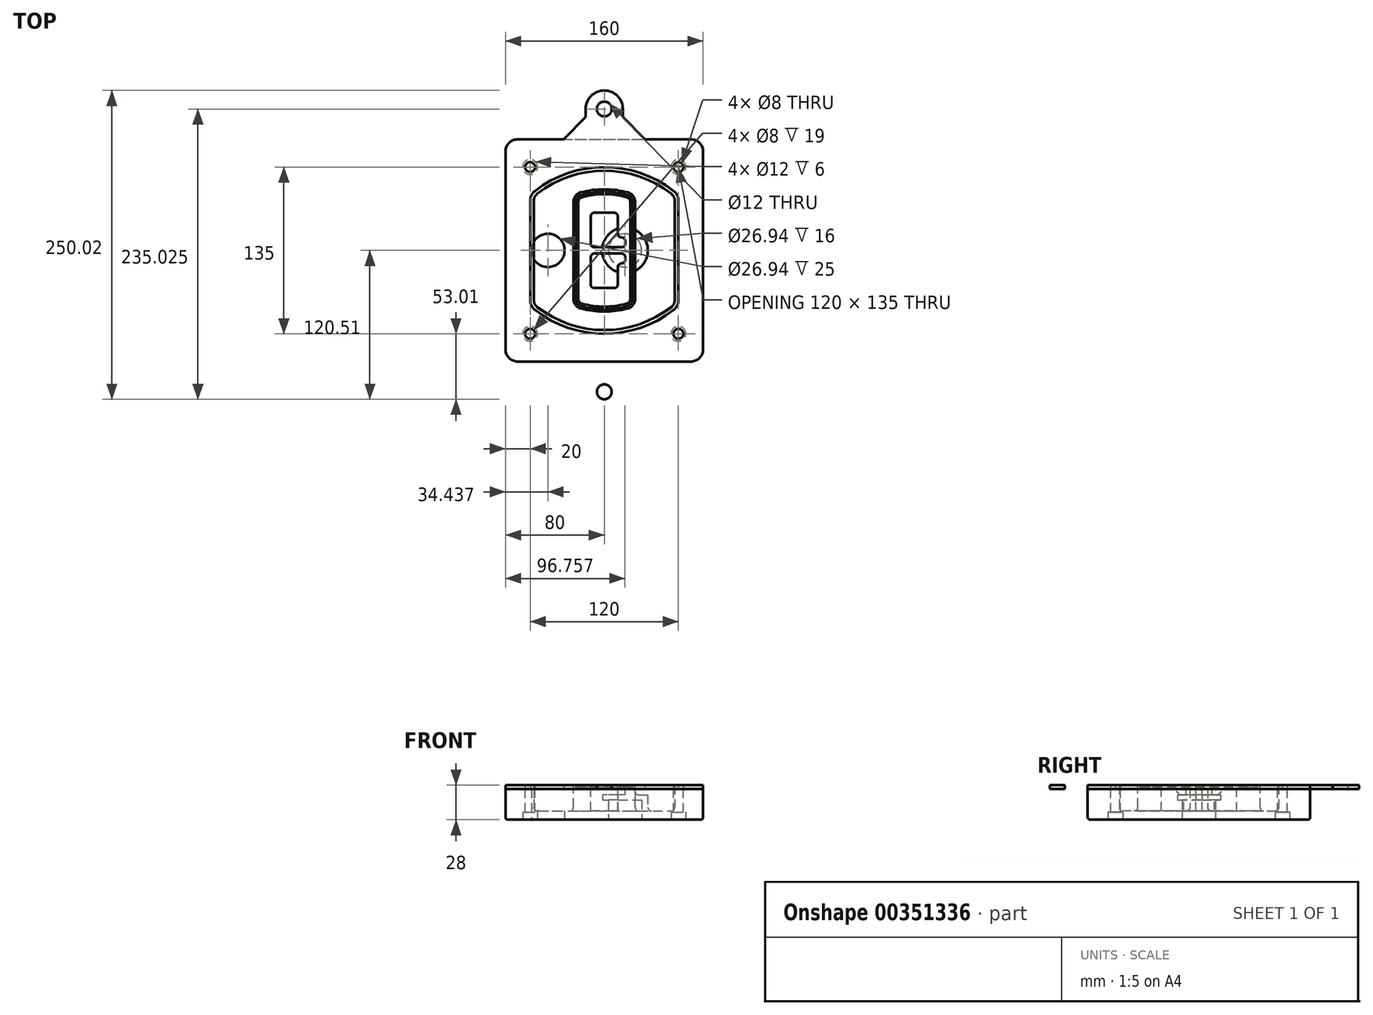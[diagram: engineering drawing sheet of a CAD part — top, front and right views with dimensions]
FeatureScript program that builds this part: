
annotation { "Feature Type Name" : "Feature", "Feature Type Description" : "" }
export const myFeature = defineFeature(function(context is Context, id is Id, definition is map)
    precondition{}
    {
        {
            var Q0;
            Q0=qCreatedBy(makeId("Top.planeOp"),FACE);
            var sketch = newSketch(context, id + "F0", { "sketchPlane" : qUnion([Q0])});
            skPoint(sketch, "E0.rect.middle", {"position": v(0, 0) * mm});
            skLineSegment(sketch, "E1.bottom", {"start": v(-70, -90) * mm, "end": v(70, -90) * mm});
            skLineSegment(sketch, "E1.top", {"start": v(-70, 90) * mm, "end": v(70, 90) * mm});
            skLineSegment(sketch, "E1.left", {"start": v(-80, -80) * mm, "end": v(-80, 80) * mm});
            skLineSegment(sketch, "E1.right", {"start": v(80, -80) * mm, "end": v(80, 80) * mm});
            skLineSegment(sketch, "E2", {"start": v(-80, 90) * mm, "end": v(80, -90) * mm, "construction": true});
            skLineSegment(sketch, "E3", {"start": v(80, 90) * mm, "end": v(-80, -90) * mm, "construction": true});
            skCircle(sketch, "E4", {"center": v(-60, 67.5) * mm, "radius": 4 * mm});
            skCircle(sketch, "E5", {"center": v(60, 67.5) * mm, "radius": 4 * mm});
            skCircle(sketch, "E6", {"center": v(60, -67.5) * mm, "radius": 4 * mm});
            skCircle(sketch, "E7", {"center": v(-60, -67.5) * mm, "radius": 4 * mm});
            skLineSegment(sketch, "E8", {"start": v(-60, 67.5) * mm, "end": v(60, 67.5) * mm, "construction": true});
            skLineSegment(sketch, "E9", {"start": v(60, 67.5) * mm, "end": v(60, -67.5) * mm, "construction": true});
            skLineSegment(sketch, "E10", {"start": v(60, -67.5) * mm, "end": v(-60, -67.5) * mm, "construction": true});
            skLineSegment(sketch, "E11", {"start": v(-60, -67.5) * mm, "end": v(-60, 67.5) * mm, "construction": true});
            skLineSegment(sketch, "E12", {"start": v(-60, 40.3) * mm, "end": v(-60, -40.3) * mm});
            skLineSegment(sketch, "E13", {"start": v(60, 40.3) * mm, "end": v(60, -40.3) * mm});
            skArc(sketch, "E14", {"start": v(56.15, 48.18) * mm, "mid": v(0, 67.5) * mm, "end": v(-56.15, 48.18) * mm});
            skArc(sketch, "E15", {"start": v(-56.15, -48.18) * mm, "mid": v(0, -67.5) * mm, "end": v(56.15, -48.18) * mm});
            skLineSegment(sketch, "E16", {"start": v(-60, 0) * mm, "end": v(60, 0) * mm, "construction": true});
            skPoint(sketch, "E17.visualSharp", {"position": v(-60, -45) * mm});
            skArc(sketch, "E17.filletArc", {"start": v(-60, -40.3) * mm, "mid": v(-58.99, -44.68) * mm, "end": v(-56.15, -48.18) * mm});
            skPoint(sketch, "E18.visualSharp", {"position": v(-60, 45) * mm});
            skArc(sketch, "E18.filletArc", {"start": v(-56.15, 48.18) * mm, "mid": v(-58.99, 44.68) * mm, "end": v(-60, 40.3) * mm});
            skPoint(sketch, "E19.visualSharp", {"position": v(60, 45) * mm});
            skArc(sketch, "E19.filletArc", {"start": v(60, 40.3) * mm, "mid": v(58.99, 44.68) * mm, "end": v(56.15, 48.18) * mm});
            skPoint(sketch, "E20.visualSharp", {"position": v(60, -45) * mm});
            skArc(sketch, "E20.filletArc", {"start": v(56.15, -48.18) * mm, "mid": v(58.99, -44.68) * mm, "end": v(60, -40.3) * mm});
            skPoint(sketch, "E21.visualSharp", {"position": v(-80, 90) * mm});
            skArc(sketch, "E21.filletArc", {"start": v(-70, 90) * mm, "mid": v(-77.07, 87.07) * mm, "end": v(-80, 80) * mm});
            skPoint(sketch, "E22.visualSharp", {"position": v(80, 90) * mm});
            skArc(sketch, "E22.filletArc", {"start": v(80, 80) * mm, "mid": v(77.07, 87.07) * mm, "end": v(70, 90) * mm});
            skPoint(sketch, "E23.visualSharp", {"position": v(80, -90) * mm});
            skArc(sketch, "E23.filletArc", {"start": v(70, -90) * mm, "mid": v(77.07, -87.07) * mm, "end": v(80, -80) * mm});
            skPoint(sketch, "E24.visualSharp", {"position": v(-80, -90) * mm});
            skArc(sketch, "E24.filletArc", {"start": v(-80, -80) * mm, "mid": v(-77.07, -87.07) * mm, "end": v(-70, -90) * mm});
            skArc(sketch, "E25.0", {"start": v(57, 40.3) * mm, "mid": v(56.3, 43.36) * mm, "end": v(54.3, 45.81) * mm});
            skLineSegment(sketch, "E25.1", {"start": v(57, 40.3) * mm, "end": v(57, -40.3) * mm});
            skArc(sketch, "E25.2", {"start": v(54.3, -45.81) * mm, "mid": v(56.3, -43.36) * mm, "end": v(57, -40.3) * mm});
            skArc(sketch, "E25.3", {"start": v(-54.3, -45.81) * mm, "mid": v(0, -64.5) * mm, "end": v(54.3, -45.81) * mm});
            skArc(sketch, "E25.4", {"start": v(-57, -40.3) * mm, "mid": v(-56.3, -43.36) * mm, "end": v(-54.3, -45.81) * mm});
            skArc(sketch, "E25.5", {"start": v(54.3, 45.81) * mm, "mid": v(0, 64.5) * mm, "end": v(-54.3, 45.81) * mm});
            skLineSegment(sketch, "E25.6", {"start": v(-57, 40.3) * mm, "end": v(-57, -40.3) * mm});
            skArc(sketch, "E25.7", {"start": v(-54.3, 45.81) * mm, "mid": v(-56.3, 43.36) * mm, "end": v(-57, 40.3) * mm});
            skArc(sketch, "E26.0", {"start": v(-58.62, 51.33) * mm, "mid": v(-62.58, 46.43) * mm, "end": v(-64, 40.3) * mm});
            skArc(sketch, "E26.1", {"start": v(58.62, 51.33) * mm, "mid": v(0, 71.5) * mm, "end": v(-58.62, 51.33) * mm});
            skArc(sketch, "E26.2", {"start": v(64, 40.3) * mm, "mid": v(62.58, 46.43) * mm, "end": v(58.62, 51.33) * mm});
            skLineSegment(sketch, "E26.3", {"start": v(64, 40.3) * mm, "end": v(64, -40.3) * mm});
            skArc(sketch, "E26.4", {"start": v(58.62, -51.33) * mm, "mid": v(62.58, -46.43) * mm, "end": v(64, -40.3) * mm});
            skLineSegment(sketch, "E26.5", {"start": v(-64, 40.3) * mm, "end": v(-64, -40.3) * mm});
            skArc(sketch, "E26.6", {"start": v(-58.62, -51.33) * mm, "mid": v(0, -71.5) * mm, "end": v(58.62, -51.33) * mm});
            skArc(sketch, "E26.7", {"start": v(-64, -40.3) * mm, "mid": v(-62.58, -46.43) * mm, "end": v(-58.62, -51.33) * mm});
            skSolve(sketch);
        }
        {
            var Q0;
            Q0=makeQuery(id+"F0.imprint","IMPRINT",FACE,{"disambiguationData":[TD([[makeQuery(id+"F0.imprint","IMPRINT",EDGE,{"derivedFrom":sQuery(id+"F0.wireOp",EDGE,"E1.bottom")}),1.0]])]});
            var Q1;
            Q1=makeQuery(id+"F0.imprint","IMPRINT",FACE,{"disambiguationData":[TD([[makeQuery(id+"F0.imprint","IMPRINT",EDGE,{"derivedFrom":sQuery(id+"F0.wireOp",EDGE,"E12")}),1.0]])]});
            var Q2;
            Q2=makeQuery(id+"F0.imprint","IMPRINT",FACE,{"disambiguationData":[TD([[makeQuery(id+"F0.imprint","IMPRINT",EDGE,{"derivedFrom":sQuery(id+"F0.wireOp",EDGE,"E25.0")}),1.0]])]});
            var Q3;
            Q3=makeQuery(id+"F0.imprint","IMPRINT",FACE,{"disambiguationData":[TD([[makeQuery(id+"F0.imprint","IMPRINT",EDGE,{"derivedFrom":sQuery(id+"F0.wireOp",EDGE,"E12")}),-1.0]])]});
            extrude(context, id + "F1", {"entities" : qUnion([Q0, Q1, Q2, Q3]), "oppositeDirection" : true, "depth" : 25 * mm});
        }
        {
            var Q0;
            Q0=makeQuery(id+"F0.imprint","IMPRINT",FACE,{"disambiguationData":[TD([[makeQuery(id+"F0.imprint","IMPRINT",EDGE,{"derivedFrom":sQuery(id+"F0.wireOp",EDGE,"E12")}),1.0]])]});
            extrude(context, id + "F2", {"entities" : qUnion([Q0]), "operationType" : NewBodyOperationType.ADD, "depth" : 3 * mm});
        }
        {
            var Q0;
            Q0=makeQuery(id+"F0.imprint","IMPRINT",FACE,{"disambiguationData":[TD([[makeQuery(id+"F0.imprint","IMPRINT",EDGE,{"derivedFrom":sQuery(id+"F0.wireOp",EDGE,"E25.0")}),1.0]])]});
            extrude(context, id + "F3", {"entities" : qUnion([Q0]), "operationType" : NewBodyOperationType.REMOVE, "oppositeDirection" : true, "depth" : 18 * mm});
        }
        {
            var Q0;
            Q0=makeQuery(id+"F2.opExtrude","CAP_FACE",FACE,{"disambiguationData":[OSD([sQuery(id+"F0.wireOp",EDGE,"E12"),sQuery(id+"F0.wireOp",EDGE,"E13"),sQuery(id+"F0.wireOp",EDGE,"E14"),sQuery(id+"F0.wireOp",EDGE,"E15"),sQuery(id+"F0.wireOp",EDGE,"E17.filletArc"),sQuery(id+"F0.wireOp",EDGE,"E18.filletArc"),sQuery(id+"F0.wireOp",EDGE,"E19.filletArc"),sQuery(id+"F0.wireOp",EDGE,"E20.filletArc"),sQuery(id+"F0.wireOp",EDGE,"E25.0"),sQuery(id+"F0.wireOp",EDGE,"E25.1"),sQuery(id+"F0.wireOp",EDGE,"E25.2"),sQuery(id+"F0.wireOp",EDGE,"E25.3"),sQuery(id+"F0.wireOp",EDGE,"E25.4"),sQuery(id+"F0.wireOp",EDGE,"E25.5"),sQuery(id+"F0.wireOp",EDGE,"E25.6"),sQuery(id+"F0.wireOp",EDGE,"E25.7")])],"isStart":false});
            var sketch = newSketch(context, id + "F4", { "sketchPlane" : qUnion([Q0])});
            skArc(sketch, "E27.0", {"start": v(-19.08, -46.97) * mm, "mid": v(0, -49.5) * mm, "end": v(19.08, -46.97) * mm});
            skArc(sketch, "E28.0", {"start": v(19.08, 46.97) * mm, "mid": v(0, 49.5) * mm, "end": v(-19.08, 46.97) * mm});
            skLineSegment(sketch, "E29", {"start": v(-25, 39.25) * mm, "end": v(-25, -39.25) * mm});
            skLineSegment(sketch, "E30", {"start": v(25, 39.25) * mm, "end": v(25, -39.25) * mm});
            skLineSegment(sketch, "E31", {"start": v(-25, 45.1) * mm, "end": v(25, 45.1) * mm, "construction": true});
            skLineSegment(sketch, "E32", {"start": v(-25, -45.1) * mm, "end": v(25, -45.1) * mm, "construction": true});
            skPoint(sketch, "E33.visualSharp", {"position": v(-25, 45.1) * mm});
            skArc(sketch, "E33.filletArc", {"start": v(-19.08, 46.97) * mm, "mid": v(-23.35, 44.11) * mm, "end": v(-25, 39.25) * mm});
            skPoint(sketch, "E34.visualSharp", {"position": v(25, 45.1) * mm});
            skArc(sketch, "E34.filletArc", {"start": v(25, 39.25) * mm, "mid": v(23.35, 44.11) * mm, "end": v(19.08, 46.97) * mm});
            skPoint(sketch, "E35.visualSharp", {"position": v(25, -45.1) * mm});
            skArc(sketch, "E35.filletArc", {"start": v(19.08, -46.97) * mm, "mid": v(23.35, -44.11) * mm, "end": v(25, -39.25) * mm});
            skPoint(sketch, "E36.visualSharp", {"position": v(-25, -45.1) * mm});
            skArc(sketch, "E36.filletArc", {"start": v(-25, -39.25) * mm, "mid": v(-23.35, -44.11) * mm, "end": v(-19.08, -46.97) * mm});
            skArc(sketch, "E37.0", {"start": v(54.3, 45.81) * mm, "mid": v(0, 64.5) * mm, "end": v(-54.3, 45.81) * mm});
            skArc(sketch, "E37.1", {"start": v(-54.3, 45.81) * mm, "mid": v(-56.3, 43.36) * mm, "end": v(-57, 40.3) * mm});
            skLineSegment(sketch, "E37.2", {"start": v(-57, 40.3) * mm, "end": v(-57, -40.3) * mm});
            skArc(sketch, "E37.3", {"start": v(-57, -40.3) * mm, "mid": v(-56.3, -43.36) * mm, "end": v(-54.3, -45.81) * mm});
            skArc(sketch, "E37.4", {"start": v(-54.3, -45.81) * mm, "mid": v(0, -64.5) * mm, "end": v(54.3, -45.81) * mm});
            skArc(sketch, "E37.5", {"start": v(54.3, -45.81) * mm, "mid": v(56.3, -43.36) * mm, "end": v(57, -40.3) * mm});
            skLineSegment(sketch, "E37.6", {"start": v(57, 40.3) * mm, "end": v(57, -40.3) * mm});
            skArc(sketch, "E37.7", {"start": v(57, 40.3) * mm, "mid": v(56.3, 43.36) * mm, "end": v(54.3, 45.81) * mm});
            skLineSegment(sketch, "E38.0", {"start": v(23, 39.25) * mm, "end": v(23, -39.25) * mm});
            skArc(sketch, "E38.1", {"start": v(18.56, -45.04) * mm, "mid": v(21.76, -42.9) * mm, "end": v(23, -39.25) * mm});
            skArc(sketch, "E38.2", {"start": v(-18.56, -45.04) * mm, "mid": v(0, -47.5) * mm, "end": v(18.56, -45.04) * mm});
            skArc(sketch, "E38.3", {"start": v(-23, -39.25) * mm, "mid": v(-21.76, -42.9) * mm, "end": v(-18.56, -45.04) * mm});
            skLineSegment(sketch, "E38.4", {"start": v(-23, 39.25) * mm, "end": v(-23, -39.25) * mm});
            skArc(sketch, "E38.5", {"start": v(23, 39.25) * mm, "mid": v(21.76, 42.9) * mm, "end": v(18.56, 45.04) * mm});
            skArc(sketch, "E38.6", {"start": v(-18.56, 45.04) * mm, "mid": v(-21.76, 42.9) * mm, "end": v(-23, 39.25) * mm});
            skArc(sketch, "E38.7", {"start": v(18.56, 45.04) * mm, "mid": v(0, 47.5) * mm, "end": v(-18.56, 45.04) * mm});
            skArc(sketch, "E39.0", {"start": v(21, 39.25) * mm, "mid": v(20.18, 41.68) * mm, "end": v(18.04, 43.1) * mm});
            skLineSegment(sketch, "E39.1", {"start": v(21, 39.25) * mm, "end": v(21, -39.25) * mm});
            skArc(sketch, "E39.2", {"start": v(18.04, -43.1) * mm, "mid": v(20.18, -41.68) * mm, "end": v(21, -39.25) * mm});
            skArc(sketch, "E39.3", {"start": v(-18.04, -43.1) * mm, "mid": v(0, -45.5) * mm, "end": v(18.04, -43.1) * mm});
            skArc(sketch, "E39.4", {"start": v(-21, -39.25) * mm, "mid": v(-20.18, -41.68) * mm, "end": v(-18.04, -43.1) * mm});
            skArc(sketch, "E39.5", {"start": v(18.04, 43.1) * mm, "mid": v(0, 45.5) * mm, "end": v(-18.04, 43.1) * mm});
            skLineSegment(sketch, "E39.6", {"start": v(-21, 39.25) * mm, "end": v(-21, -39.25) * mm});
            skArc(sketch, "E39.7", {"start": v(-18.04, 43.1) * mm, "mid": v(-20.18, 41.68) * mm, "end": v(-21, 39.25) * mm});
            skLineSegment(sketch, "E40", {"start": v(-25, 0) * mm, "end": v(25, 0) * mm, "construction": true});
            skLineSegment(sketch, "E41", {"start": v(-11, 5.5) * mm, "end": v(-11, 27.5) * mm});
            skLineSegment(sketch, "E42", {"start": v(-8, 30.5) * mm, "end": v(8, 30.5) * mm});
            skLineSegment(sketch, "E43", {"start": v(11, 27.5) * mm, "end": v(11, 13.5) * mm});
            skLineSegment(sketch, "E44", {"start": v(14, 10.5) * mm, "end": v(14, 10.5) * mm});
            skLineSegment(sketch, "E45", {"start": v(17, 7.5) * mm, "end": v(17, 5.5) * mm});
            skLineSegment(sketch, "E46", {"start": v(14, 2.5) * mm, "end": v(-8, 2.5) * mm});
            skPoint(sketch, "E47.visualSharp", {"position": v(-11, 30.5) * mm});
            skArc(sketch, "E47.filletArc", {"start": v(-8, 30.5) * mm, "mid": v(-10.12, 29.62) * mm, "end": v(-11, 27.5) * mm});
            skPoint(sketch, "E48.visualSharp", {"position": v(11, 30.5) * mm});
            skArc(sketch, "E48.filletArc", {"start": v(11, 27.5) * mm, "mid": v(10.12, 29.62) * mm, "end": v(8, 30.5) * mm});
            skPoint(sketch, "E49.visualSharp", {"position": v(11, 10.5) * mm});
            skArc(sketch, "E49.filletArc", {"start": v(11, 13.5) * mm, "mid": v(11.88, 11.38) * mm, "end": v(14, 10.5) * mm});
            skPoint(sketch, "E50.visualSharp", {"position": v(17, 10.5) * mm});
            skArc(sketch, "E50.filletArc", {"start": v(17, 7.5) * mm, "mid": v(16.12, 9.62) * mm, "end": v(14, 10.5) * mm});
            skPoint(sketch, "E51.visualSharp", {"position": v(17, 2.5) * mm});
            skArc(sketch, "E51.filletArc", {"start": v(14, 2.5) * mm, "mid": v(16.12, 3.38) * mm, "end": v(17, 5.5) * mm});
            skPoint(sketch, "E52.visualSharp", {"position": v(-11, 2.5) * mm});
            skArc(sketch, "E52.filletArc", {"start": v(-11, 5.5) * mm, "mid": v(-10.12, 3.38) * mm, "end": v(-8, 2.5) * mm});
            skLineSegment(sketch, "E53.0.MirrorCS", {"start": v(14, -2.5) * mm, "end": v(-8, -2.5) * mm});
            skArc(sketch, "E54.0.MirrorCS", {"start": v(-11, -5.5) * mm, "mid": v(-10.12, -3.38) * mm, "end": v(-8, -2.5) * mm});
            skLineSegment(sketch, "E55.0.MirrorCS", {"start": v(-11, -5.5) * mm, "end": v(-11, -27.5) * mm});
            skArc(sketch, "E56.0.MirrorCS", {"start": v(-8, -30.5) * mm, "mid": v(-10.12, -29.62) * mm, "end": v(-11, -27.5) * mm});
            skLineSegment(sketch, "E57.0.MirrorCS", {"start": v(-8, -30.5) * mm, "end": v(8, -30.5) * mm});
            skArc(sketch, "E58.0.MirrorCS", {"start": v(11, -27.5) * mm, "mid": v(10.12, -29.62) * mm, "end": v(8, -30.5) * mm});
            skLineSegment(sketch, "E59.0.MirrorCS", {"start": v(11, -27.5) * mm, "end": v(11, -13.5) * mm});
            skArc(sketch, "E60.0.MirrorCS", {"start": v(11, -13.5) * mm, "mid": v(11.88, -11.38) * mm, "end": v(14, -10.5) * mm});
            skArc(sketch, "E61.0.MirrorCS", {"start": v(17, -7.5) * mm, "mid": v(16.12, -9.62) * mm, "end": v(14, -10.5) * mm});
            skLineSegment(sketch, "E62.0.MirrorCS", {"start": v(17, -7.5) * mm, "end": v(17, -5.5) * mm});
            skArc(sketch, "E63.0.MirrorCS", {"start": v(14, -2.5) * mm, "mid": v(16.12, -3.38) * mm, "end": v(17, -5.5) * mm});
            skSolve(sketch);
        }
        {
            var Q0;
            Q0=makeQuery(id+"F4.imprint","IMPRINT",FACE,{"disambiguationData":[TD([[makeQuery(id+"F4.imprint","IMPRINT",EDGE,{"derivedFrom":sQuery(id+"F4.wireOp",EDGE,"E27.0")}),1.0]])]});
            var Q1;
            Q1=makeQuery(id+"F4.imprint","IMPRINT",FACE,{"disambiguationData":[TD([[makeQuery(id+"F4.imprint","IMPRINT",EDGE,{"derivedFrom":sQuery(id+"F4.wireOp",EDGE,"E38.0")}),-1.0]])]});
            var Q2;
            Q2=makeQuery(id+"F4.imprint","IMPRINT",FACE,{"disambiguationData":[TD([[makeQuery(id+"F4.imprint","IMPRINT",EDGE,{"derivedFrom":sQuery(id+"F4.wireOp",EDGE,"E39.0")}),1.0]])]});
            extrude(context, id + "F5", {"entities" : qUnion([Q0, Q1, Q2]), "operationType" : NewBodyOperationType.ADD, "endBound" : BoundingType.UP_TO_NEXT, "oppositeDirection" : true, "depth" : 25 * mm});
        }
        {
            var Q0;
            Q0=makeQuery(id+"F4.imprint","IMPRINT",FACE,{"disambiguationData":[TD([[makeQuery(id+"F4.imprint","IMPRINT",EDGE,{"derivedFrom":sQuery(id+"F4.wireOp",EDGE,"E38.0")}),-1.0]])]});
            extrude(context, id + "F6", {"entities" : qUnion([Q0]), "operationType" : NewBodyOperationType.REMOVE, "oppositeDirection" : true, "depth" : 2 * mm});
        }
        {
            var Q0;
            Q0=makeQuery(id+"F1.opExtrude","CAP_FACE",FACE,{"disambiguationData":[OSD([sQuery(id+"F0.wireOp",EDGE,"E1.bottom"),sQuery(id+"F0.wireOp",EDGE,"E1.top"),sQuery(id+"F0.wireOp",EDGE,"E1.left"),sQuery(id+"F0.wireOp",EDGE,"E1.right"),sQuery(id+"F0.wireOp",EDGE,"E4"),sQuery(id+"F0.wireOp",EDGE,"E5"),sQuery(id+"F0.wireOp",EDGE,"E6"),sQuery(id+"F0.wireOp",EDGE,"E7"),sQuery(id+"F0.wireOp",EDGE,"E21.filletArc"),sQuery(id+"F0.wireOp",EDGE,"E22.filletArc"),sQuery(id+"F0.wireOp",EDGE,"E23.filletArc"),sQuery(id+"F0.wireOp",EDGE,"E24.filletArc")])],"isStart":false});
            var sketch = newSketch(context, id + "F7", { "sketchPlane" : qUnion([Q0])});
            skCircle(sketch, "E64", {"center": v(16.76, 0) * mm, "radius": 13.47 * mm});
            skCircle(sketch, "E65", {"center": v(-45.56, 0) * mm, "radius": 13.47 * mm});
            skLineSegment(sketch, "E66", {"start": v(80, 0) * mm, "end": v(-80, 0) * mm});
            skCircle(sketch, "E67", {"center": v(16.76, 0) * mm, "radius": 18.47 * mm});
            skCircle(sketch, "E68", {"center": v(60, -67.5) * mm, "radius": 6 * mm});
            skCircle(sketch, "E69", {"center": v(-60, -67.5) * mm, "radius": 6 * mm});
            skCircle(sketch, "E70", {"center": v(-60, 67.5) * mm, "radius": 6 * mm});
            skCircle(sketch, "E71", {"center": v(60, 67.5) * mm, "radius": 6 * mm});
            skSolve(sketch);
        }
        {
            var Q0;
            {var subQ1=sQuery(id+"F7.wireOp",EDGE,"E66");var subQ4=sQuery(id+"F7.wireOp",EDGE,"E64");var subQ6=makeQuery(id+"F7.imprint","INTERSECT",VERTEX,{"disambiguationData":[OD(0.0)],"derivedFrom":[subQ4,subQ1]});Q0=makeQuery(id+"F7.imprint","IMPRINT",FACE,{"disambiguationData":[TD([[makeQuery(id+"F7.imprint","IMPRINT",EDGE,{"disambiguationData":[TD([[subQ6,-1.0]])],"derivedFrom":subQ4}),-1.0]])]});}
            var Q1;
            {var subQ0=sQuery(id+"F7.wireOp",EDGE,"E66");var subQ1=sQuery(id+"F7.wireOp",EDGE,"E64");var subQ3=makeQuery(id+"F7.imprint","INTERSECT",VERTEX,{"disambiguationData":[OD(0.0)],"derivedFrom":[subQ1,subQ0]});Q1=makeQuery(id+"F7.imprint","IMPRINT",FACE,{"disambiguationData":[TD([[makeQuery(id+"F7.imprint","IMPRINT",EDGE,{"disambiguationData":[TD([[subQ3,-1.0]])],"derivedFrom":subQ1}),1.0]])]});}
            var Q2;
            {var subQ0=sQuery(id+"F7.wireOp",EDGE,"E66");var subQ1=sQuery(id+"F7.wireOp",EDGE,"E64");var subQ3=makeQuery(id+"F7.imprint","INTERSECT",VERTEX,{"disambiguationData":[OD(0.0)],"derivedFrom":[subQ1,subQ0]});Q2=makeQuery(id+"F7.imprint","IMPRINT",FACE,{"disambiguationData":[TD([[makeQuery(id+"F7.imprint","IMPRINT",EDGE,{"disambiguationData":[TD([[subQ3,1.0]])],"derivedFrom":subQ1}),1.0]])]});}
            var Q3;
            {var subQ1=sQuery(id+"F7.wireOp",EDGE,"E66");var subQ4=sQuery(id+"F7.wireOp",EDGE,"E64");var subQ6=makeQuery(id+"F7.imprint","INTERSECT",VERTEX,{"disambiguationData":[OD(0.0)],"derivedFrom":[subQ4,subQ1]});Q3=makeQuery(id+"F7.imprint","IMPRINT",FACE,{"disambiguationData":[TD([[makeQuery(id+"F7.imprint","IMPRINT",EDGE,{"disambiguationData":[TD([[subQ6,1.0]])],"derivedFrom":subQ4}),-1.0]])]});}
            extrude(context, id + "F8", {"entities" : qUnion([Q0, Q1, Q2, Q3]), "operationType" : NewBodyOperationType.ADD, "oppositeDirection" : true, "depth" : 20 * mm});
        }
        {
            var Q0;
            {var subQ0=sQuery(id+"F7.wireOp",EDGE,"E66");var subQ1=sQuery(id+"F7.wireOp",EDGE,"E64");var subQ3=makeQuery(id+"F7.imprint","INTERSECT",VERTEX,{"disambiguationData":[OD(0.0)],"derivedFrom":[subQ1,subQ0]});Q0=makeQuery(id+"F7.imprint","IMPRINT",FACE,{"disambiguationData":[TD([[makeQuery(id+"F7.imprint","IMPRINT",EDGE,{"disambiguationData":[TD([[subQ3,-1.0]])],"derivedFrom":subQ1}),1.0]])]});}
            var Q1;
            {var subQ0=sQuery(id+"F7.wireOp",EDGE,"E66");var subQ1=sQuery(id+"F7.wireOp",EDGE,"E64");var subQ3=makeQuery(id+"F7.imprint","INTERSECT",VERTEX,{"disambiguationData":[OD(0.0)],"derivedFrom":[subQ1,subQ0]});Q1=makeQuery(id+"F7.imprint","IMPRINT",FACE,{"disambiguationData":[TD([[makeQuery(id+"F7.imprint","IMPRINT",EDGE,{"disambiguationData":[TD([[subQ3,1.0]])],"derivedFrom":subQ1}),1.0]])]});}
            extrude(context, id + "F9", {"entities" : qUnion([Q0, Q1]), "operationType" : NewBodyOperationType.REMOVE, "oppositeDirection" : true, "depth" : 16 * mm});
        }
        {
            var Q0;
            {var subQ0=sQuery(id+"F7.wireOp",EDGE,"E66");var subQ1=sQuery(id+"F7.wireOp",EDGE,"E65");var subQ3=makeQuery(id+"F7.imprint","INTERSECT",VERTEX,{"disambiguationData":[OD(0.0)],"derivedFrom":[subQ1,subQ0]});Q0=makeQuery(id+"F7.imprint","IMPRINT",FACE,{"disambiguationData":[TD([[makeQuery(id+"F7.imprint","IMPRINT",EDGE,{"disambiguationData":[TD([[subQ3,-1.0]])],"derivedFrom":subQ1}),1.0]])]});}
            var Q1;
            {var subQ0=sQuery(id+"F7.wireOp",EDGE,"E66");var subQ1=sQuery(id+"F7.wireOp",EDGE,"E65");var subQ3=makeQuery(id+"F7.imprint","INTERSECT",VERTEX,{"disambiguationData":[OD(0.0)],"derivedFrom":[subQ1,subQ0]});Q1=makeQuery(id+"F7.imprint","IMPRINT",FACE,{"disambiguationData":[TD([[makeQuery(id+"F7.imprint","IMPRINT",EDGE,{"disambiguationData":[TD([[subQ3,1.0]])],"derivedFrom":subQ1}),1.0]])]});}
            extrude(context, id + "F10", {"entities" : qUnion([Q0, Q1]), "operationType" : NewBodyOperationType.REMOVE, "oppositeDirection" : true, "depth" : 25 * mm});
        }
        {
            var Q0;
            Q0=makeQuery(id+"F7.imprint","IMPRINT",FACE,{"disambiguationData":[TD([[makeQuery(id+"F7.imprint","IMPRINT",EDGE,{"derivedFrom":sQuery(id+"F7.wireOp",EDGE,"E68")}),1.0]])]});
            var Q1;
            Q1=makeQuery(id+"F7.imprint","IMPRINT",FACE,{"disambiguationData":[TD([[makeQuery(id+"F7.imprint","IMPRINT",EDGE,{"derivedFrom":makeQuery(id+"F1.opExtrude","CAP_EDGE",EDGE,{"disambiguationData":[OSD([sQuery(id+"F0.wireOp",EDGE,"E5")])],"isStart":false})}),-1.0]])]});
            var Q2;
            Q2=makeQuery(id+"F7.imprint","IMPRINT",FACE,{"disambiguationData":[TD([[makeQuery(id+"F7.imprint","IMPRINT",EDGE,{"derivedFrom":sQuery(id+"F7.wireOp",EDGE,"E69")}),1.0]])]});
            var Q3;
            Q3=makeQuery(id+"F7.imprint","IMPRINT",FACE,{"disambiguationData":[TD([[makeQuery(id+"F7.imprint","IMPRINT",EDGE,{"derivedFrom":makeQuery(id+"F1.opExtrude","CAP_EDGE",EDGE,{"disambiguationData":[OSD([sQuery(id+"F0.wireOp",EDGE,"E4")])],"isStart":false})}),-1.0]])]});
            var Q4;
            Q4=makeQuery(id+"F7.imprint","IMPRINT",FACE,{"disambiguationData":[TD([[makeQuery(id+"F7.imprint","IMPRINT",EDGE,{"derivedFrom":sQuery(id+"F7.wireOp",EDGE,"E70")}),1.0]])]});
            var Q5;
            Q5=makeQuery(id+"F7.imprint","IMPRINT",FACE,{"disambiguationData":[TD([[makeQuery(id+"F7.imprint","IMPRINT",EDGE,{"derivedFrom":makeQuery(id+"F1.opExtrude","CAP_EDGE",EDGE,{"disambiguationData":[OSD([sQuery(id+"F0.wireOp",EDGE,"E7")])],"isStart":false})}),-1.0]])]});
            var Q6;
            Q6=makeQuery(id+"F7.imprint","IMPRINT",FACE,{"disambiguationData":[TD([[makeQuery(id+"F7.imprint","IMPRINT",EDGE,{"derivedFrom":sQuery(id+"F7.wireOp",EDGE,"E71")}),1.0]])]});
            var Q7;
            Q7=makeQuery(id+"F7.imprint","IMPRINT",FACE,{"disambiguationData":[TD([[makeQuery(id+"F7.imprint","IMPRINT",EDGE,{"derivedFrom":makeQuery(id+"F1.opExtrude","CAP_EDGE",EDGE,{"disambiguationData":[OSD([sQuery(id+"F0.wireOp",EDGE,"E6")])],"isStart":false})}),-1.0]])]});
            extrude(context, id + "F11", {"entities" : qUnion([Q0, Q1, Q2, Q3, Q4, Q5, Q6, Q7]), "operationType" : NewBodyOperationType.REMOVE, "oppositeDirection" : true, "depth" : 6 * mm});
        }
        {
            var Q0;
            Q0=makeQuery(id+"F9.boolean.opBoolean","COPY",FACE,{"derivedFrom":makeQuery(id+"F9.opExtrude","CAP_FACE",FACE,{"disambiguationData":[OSD([sQuery(id+"F7.wireOp",EDGE,"E64")])],"isStart":false})});
            var sketch = newSketch(context, id + "F12", { "sketchPlane" : qUnion([Q0])});
            skArc(sketch, "E72.0", {"start": v(11, 17.55) * mm, "mid": v(2.57, 11.82) * mm, "end": v(-1.54, 2.5) * mm});
            skArc(sketch, "E72.1", {"start": v(-1.54, -2.5) * mm, "mid": v(2.57, -11.82) * mm, "end": v(11, -17.55) * mm});
            skLineSegment(sketch, "E73", {"start": v(-1.54, -2.5) * mm, "end": v(14, -2.5) * mm});
            skLineSegment(sketch, "E74.0", {"start": v(14, 2.5) * mm, "end": v(-1.54, 2.5) * mm});
            skArc(sketch, "E74.1", {"start": v(14, 2.5) * mm, "mid": v(16.12, 3.38) * mm, "end": v(17, 5.5) * mm});
            skLineSegment(sketch, "E74.2", {"start": v(17, 7.5) * mm, "end": v(17, 5.5) * mm});
            skArc(sketch, "E74.3", {"start": v(17, 7.5) * mm, "mid": v(16.12, 9.62) * mm, "end": v(14, 10.5) * mm});
            skArc(sketch, "E74.4", {"start": v(11, 13.5) * mm, "mid": v(11.88, 11.38) * mm, "end": v(14, 10.5) * mm});
            skLineSegment(sketch, "E74.5", {"start": v(11, 17.55) * mm, "end": v(11, 13.5) * mm});
            skLineSegment(sketch, "E74.7", {"start": v(14, -2.5) * mm, "end": v(-1.54, -2.5) * mm});
            skArc(sketch, "E74.8", {"start": v(14, -2.5) * mm, "mid": v(16.12, -3.38) * mm, "end": v(17, -5.5) * mm});
            skLineSegment(sketch, "E74.9", {"start": v(17, -7.5) * mm, "end": v(17, -5.5) * mm});
            skArc(sketch, "E74.10", {"start": v(17, -7.5) * mm, "mid": v(16.12, -9.62) * mm, "end": v(14, -10.5) * mm});
            skArc(sketch, "E74.11", {"start": v(11, -13.5) * mm, "mid": v(11.88, -11.38) * mm, "end": v(14, -10.5) * mm});
            skLineSegment(sketch, "E74.12", {"start": v(11, -17.55) * mm, "end": v(11, -13.5) * mm});
            skPoint(sketch, "E75.orphan", {"position": v(11, -27.5) * mm});
            skPoint(sketch, "E76.orphan", {"position": v(-8, -2.5) * mm});
            skPoint(sketch, "E77.orphan", {"position": v(-8, 2.5) * mm});
            skPoint(sketch, "E78.orphan", {"position": v(11, 27.5) * mm});
            skSolve(sketch);
        }
        {
            var Q0;
            {var subQ7=sQuery(id+"F12.wireOp",EDGE,"E72.0");var subQ14=sQuery(id+"F12.wireOp",EDGE,"E72.1");var subQ16=sQuery(id+"F12.wireOp",EDGE,"E74.1");var subQ18=sQuery(id+"F12.wireOp",EDGE,"E74.8");Q0=qUnion([makeQuery(id+"F12.imprint","IMPRINT",FACE,{"disambiguationData":[TD([[makeQuery(id+"F12.imprint","IMPRINT",EDGE,{"derivedFrom":subQ7}),1.0]])]}),makeQuery(id+"F12.imprint","IMPRINT",FACE,{"disambiguationData":[TD([[makeQuery(id+"F12.imprint","IMPRINT",EDGE,{"derivedFrom":subQ14}),1.0]])]}),makeQuery(id+"F12.imprint","IMPRINT",FACE,{"disambiguationData":[TD([[makeQuery(id+"F12.imprint","IMPRINT",EDGE,{"derivedFrom":subQ16}),1.0]])]}),makeQuery(id+"F12.imprint","IMPRINT",FACE,{"disambiguationData":[TD([[makeQuery(id+"F12.imprint","IMPRINT",EDGE,{"derivedFrom":subQ18}),-1.0]])]})]);}
            var Q1;
            Q1=makeQuery(id+"F5.boolean.opBoolean","SPLIT",FACE,{"disambiguationData":[TD([makeQuery(id+"F5.opExtrude","SWEPT_FACE",FACE,{"disambiguationData":[OSD([sQuery(id+"F4.wireOp",EDGE,"E41")])]})])],"derivedFrom":makeQuery(id+"F3.boolean.opBoolean","COPY",FACE,{"derivedFrom":makeQuery(id+"F3.opExtrude","CAP_FACE",FACE,{"disambiguationData":[OSD([sQuery(id+"F0.wireOp",EDGE,"E25.0"),sQuery(id+"F0.wireOp",EDGE,"E25.1"),sQuery(id+"F0.wireOp",EDGE,"E25.2"),sQuery(id+"F0.wireOp",EDGE,"E25.3"),sQuery(id+"F0.wireOp",EDGE,"E25.4"),sQuery(id+"F0.wireOp",EDGE,"E25.5"),sQuery(id+"F0.wireOp",EDGE,"E25.6"),sQuery(id+"F0.wireOp",EDGE,"E25.7")])],"isStart":false})})});
            extrude(context, id + "F13", {"entities" : qUnion([Q0]), "operationType" : NewBodyOperationType.REMOVE, "endBound" : BoundingType.UP_TO_SURFACE, "endBoundEntityFace" : qUnion([Q1]), "depth" : 25 * mm});
        }
        {
            var Q0;
            Q0=makeQuery(id+"F3.boolean.opBoolean","COPY",EDGE,{"derivedFrom":makeQuery(id+"F3.opExtrude","CAP_EDGE",EDGE,{"disambiguationData":[OSD([sQuery(id+"F0.wireOp",EDGE,"E25.6")])],"isStart":false})});
            var Q1;
            Q1=makeQuery(id+"F8.boolean.opBoolean","INTERSECT",EDGE,{"derivedFrom":[makeQuery(id+"F5.opExtrude","SWEPT_FACE",FACE,{"disambiguationData":[OSD([sQuery(id+"F4.wireOp",EDGE,"E30")])]}),makeQuery(id+"F8.opExtrude","CAP_FACE",FACE,{"disambiguationData":[OSD([sQuery(id+"F7.wireOp",EDGE,"E67")])],"isStart":false})]});
            var Q2;
            Q2=makeQuery(id+"F8.boolean.opBoolean","INTERSECT",EDGE,{"disambiguationData":[OD(1.0)],"derivedFrom":[makeQuery(id+"F5.opExtrude","SWEPT_FACE",FACE,{"disambiguationData":[OSD([sQuery(id+"F4.wireOp",EDGE,"E30")])]}),makeQuery(id+"F8.opExtrude","SWEPT_FACE",FACE,{"disambiguationData":[OSD([sQuery(id+"F7.wireOp",EDGE,"E67")])]})]});
            var Q3;
            {var subQ0=sQuery(id+"F4.wireOp",EDGE,"E30");Q3=makeQuery(id+"F8.boolean.opBoolean","SPLIT",EDGE,{"disambiguationData":[TD([makeQuery(id+"F5.opExtrude","SWEPT_FACE",FACE,{"disambiguationData":[OSD([sQuery(id+"F4.wireOp",EDGE,"E35.filletArc")])]})])],"derivedFrom":makeQuery(id+"F5.opExtrude","CAP_EDGE",EDGE,{"disambiguationData":[OSD([subQ0])],"isStart":false})});}
            var Q4;
            {var subQ0=sQuery(id+"F0.wireOp",EDGE,"E25.7");var subQ1=sQuery(id+"F0.wireOp",EDGE,"E25.1");var subQ2=sQuery(id+"F0.wireOp",EDGE,"E25.6");var subQ3=sQuery(id+"F0.wireOp",EDGE,"E25.5");var subQ4=sQuery(id+"F0.wireOp",EDGE,"E25.4");var subQ5=sQuery(id+"F0.wireOp",EDGE,"E25.0");var subQ6=sQuery(id+"F0.wireOp",EDGE,"E25.2");var subQ7=sQuery(id+"F0.wireOp",EDGE,"E25.3");Q4=makeQuery(id+"F8.boolean.opBoolean","INTERSECT",EDGE,{"derivedFrom":[makeQuery(id+"F5.boolean.opBoolean","SPLIT",FACE,{"disambiguationData":[TD([makeQuery(id+"F2.opExtrude","SWEPT_FACE",FACE,{"disambiguationData":[OSD([subQ5])]})])],"derivedFrom":makeQuery(id+"F3.boolean.opBoolean","COPY",FACE,{"derivedFrom":makeQuery(id+"F3.opExtrude","CAP_FACE",FACE,{"disambiguationData":[OSD([subQ5,subQ1,subQ6,subQ7,subQ4,subQ3,subQ2,subQ0])],"isStart":false})})}),makeQuery(id+"F8.opExtrude","SWEPT_FACE",FACE,{"disambiguationData":[OSD([sQuery(id+"F7.wireOp",EDGE,"E67")])]})]});}
            var Q5;
            Q5=makeQuery(id+"F8.boolean.opBoolean","INTERSECT",EDGE,{"disambiguationData":[OD(0.0)],"derivedFrom":[makeQuery(id+"F5.opExtrude","SWEPT_FACE",FACE,{"disambiguationData":[OSD([sQuery(id+"F4.wireOp",EDGE,"E30")])]}),makeQuery(id+"F8.opExtrude","SWEPT_FACE",FACE,{"disambiguationData":[OSD([sQuery(id+"F7.wireOp",EDGE,"E67")])]})]});
            fillet(context, id + "F14", {"entities" : qUnion([Q0, Q1, Q2, Q3, Q4, Q5]), "radius" : 3 * mm, "tangentPropagation" : true, "allowEdgeOverflow" : false});
        }
        {
            var Q0;
            Q0=makeQuery(id+"F1.opExtrude","CAP_EDGE",EDGE,{"disambiguationData":[OSD([sQuery(id+"F0.wireOp",EDGE,"E1.bottom")])],"isStart":false});
            fillet(context, id + "F15", {"entities" : qUnion([Q0]), "radius" : 2 * mm, "tangentPropagation" : true, "allowEdgeOverflow" : false});
        }
        {
            var Q0;
            {var subQ0=sQuery(id+"F0.wireOp",EDGE,"E21.filletArc");var subQ1=sQuery(id+"F0.wireOp",EDGE,"E7");var subQ2=sQuery(id+"F0.wireOp",EDGE,"E6");var subQ3=sQuery(id+"F0.wireOp",EDGE,"E5");var subQ4=sQuery(id+"F0.wireOp",EDGE,"E4");var subQ5=sQuery(id+"F0.wireOp",EDGE,"E22.filletArc");var subQ6=sQuery(id+"F0.wireOp",EDGE,"E1.bottom");var subQ7=sQuery(id+"F0.wireOp",EDGE,"E1.right");var subQ8=sQuery(id+"F0.wireOp",EDGE,"E1.top");var subQ9=sQuery(id+"F0.wireOp",EDGE,"E1.left");var subQ10=sQuery(id+"F0.wireOp",EDGE,"E23.filletArc");var subQ11=sQuery(id+"F0.wireOp",EDGE,"E24.filletArc");Q0=makeQuery(id+"F2.boolean.opBoolean","SPLIT",FACE,{"disambiguationData":[TD([makeQuery(id+"F1.opExtrude","SWEPT_FACE",FACE,{"disambiguationData":[OSD([subQ6])]})])],"derivedFrom":makeQuery(id+"F1.opExtrude","CAP_FACE",FACE,{"disambiguationData":[OSD([subQ6,subQ8,subQ9,subQ7,subQ4,subQ3,subQ2,subQ1,subQ0,subQ5,subQ10,subQ11])],"isStart":true})});}
            var sketch = newSketch(context, id + "F16", { "sketchPlane" : qUnion([Q0])});
            skLineSegment(sketch, "E79", {"start": v(-33, 90) * mm, "end": v(-15, 108) * mm});
            skLineSegment(sketch, "E80", {"start": v(-15, 108) * mm, "end": v(-15, 114.51) * mm});
            skArc(sketch, "E81", {"start": v(15, 114.51) * mm, "mid": v(0, 129.51) * mm, "end": v(-15, 114.51) * mm});
            skLineSegment(sketch, "E82", {"start": v(15, 114.51) * mm, "end": v(15, 108) * mm});
            skLineSegment(sketch, "E83", {"start": v(15, 108) * mm, "end": v(33, 90) * mm});
            skCircle(sketch, "E84", {"center": v(0, 114.51) * mm, "radius": 6 * mm});
            skLineSegment(sketch, "E85", {"start": v(0, 114.51) * mm, "end": v(0, 90) * mm, "construction": true});
            skPoint(sketch, "E85.endSnap0", {"position": v(0, 90) * mm});
            skLineSegment(sketch, "E86", {"start": v(-80, 0) * mm, "end": v(80, 0) * mm, "construction": true});
            skCircle(sketch, "E87.MirrorC", {"center": v(0, -114.51) * mm, "radius": 6 * mm});
            skArc(sketch, "E88.MirrorCS", {"start": v(15, -114.51) * mm, "mid": v(0, -129.51) * mm, "end": v(-15, -114.51) * mm});
            skLineSegment(sketch, "E89.MirrorCS", {"start": v(15, -108) * mm, "end": v(33, -90) * mm});
            skLineSegment(sketch, "E90.MirrorCS", {"start": v(0, -114.51) * mm, "end": v(0, -90) * mm, "construction": true});
            skLineSegment(sketch, "E91.MirrorCS", {"start": v(-33, -90) * mm, "end": v(-15, -108) * mm});
            skLineSegment(sketch, "E92.MirrorCS", {"start": v(-15, -108) * mm, "end": v(-15, -114.51) * mm});
            skLineSegment(sketch, "E93.MirrorCS", {"start": v(15, -114.51) * mm, "end": v(15, -108) * mm});
            skSolve(sketch);
        }
        {
            var Q0;
            {var subQ0=sQuery(id+"F16.wireOp",EDGE,"E79");Q0=makeQuery(id+"F16.imprint","IMPRINT",FACE,{"disambiguationData":[TD([[makeQuery(id+"F16.imprint","IMPRINT",EDGE,{"derivedFrom":subQ0}),-1.0]])]});}
            var Q1;
            Q1=makeQuery(id+"F16.imprint","IMPRINT",FACE,{"disambiguationData":[TD([[makeQuery(id+"F16.imprint","IMPRINT",EDGE,{"derivedFrom":makeQuery(id+"F1.opExtrude","CAP_EDGE",EDGE,{"disambiguationData":[OSD([sQuery(id+"F0.wireOp",EDGE,"E1.left")])],"isStart":true})}),-1.0]])]});
            var Q2;
            Q2=makeQuery(id+"F16.imprint","IMPRINT",FACE,{"disambiguationData":[TD([[makeQuery(id+"F16.imprint","IMPRINT",EDGE,{"derivedFrom":sQuery(id+"F16.wireOp",EDGE,"E87.MirrorC")}),1.0]])]});
            var Q3;
            Q3=makeQuery(id+"F2.opExtrude","CAP_FACE",FACE,{"disambiguationData":[OSD([sQuery(id+"F0.wireOp",EDGE,"E12"),sQuery(id+"F0.wireOp",EDGE,"E13"),sQuery(id+"F0.wireOp",EDGE,"E14"),sQuery(id+"F0.wireOp",EDGE,"E15"),sQuery(id+"F0.wireOp",EDGE,"E17.filletArc"),sQuery(id+"F0.wireOp",EDGE,"E18.filletArc"),sQuery(id+"F0.wireOp",EDGE,"E19.filletArc"),sQuery(id+"F0.wireOp",EDGE,"E20.filletArc"),sQuery(id+"F0.wireOp",EDGE,"E25.0"),sQuery(id+"F0.wireOp",EDGE,"E25.1"),sQuery(id+"F0.wireOp",EDGE,"E25.2"),sQuery(id+"F0.wireOp",EDGE,"E25.3"),sQuery(id+"F0.wireOp",EDGE,"E25.4"),sQuery(id+"F0.wireOp",EDGE,"E25.5"),sQuery(id+"F0.wireOp",EDGE,"E25.6"),sQuery(id+"F0.wireOp",EDGE,"E25.7")])],"isStart":false});
            extrude(context, id + "F17", {"entities" : qUnion([Q0, Q1, Q2]), "endBound" : BoundingType.UP_TO_SURFACE, "endBoundEntityFace" : qUnion([Q3]), "depth" : 25 * mm});
        }
    });
